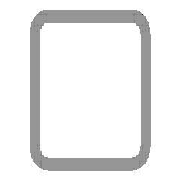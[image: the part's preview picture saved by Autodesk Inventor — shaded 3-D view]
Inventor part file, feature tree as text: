
AUTODESK INVENTOR PART (.ipt)
format: ipt  version: 2025.1 (Build 291241020, 241B)  size: 142,848 bytes
history: native  units: mm (DEFAULTED — no unit token found)
features: other x4, sketch x1, plane x1
ambient origin geometry x8: Origin, YZ Plane, XZ Plane, XY Plane, X Axis, Y Axis, Z Axis, Center Point
bodies: Solid1 (feature_tree), Body (feature_tree)
feature tree (6):
  parser-record x1  (decoder bookkeeping rows leaked as tree rows — omitted from the tree; the rows remain in map.json)
  other  "Driven Length"
  other  "Start plane"
  other  "End plane"
  sketch  "Sketch3"  dims[d3=2400.0mm d4=0.0mm d7=8.0mm d9=100.0mm d11=100.0mm d12=4.0mm d13=-0.0mm d14=2400.0mm d15=50.0mm d16=50.0mm d17=90.0deg d18=2400.0mm]
  plane  "Work Plane3"
